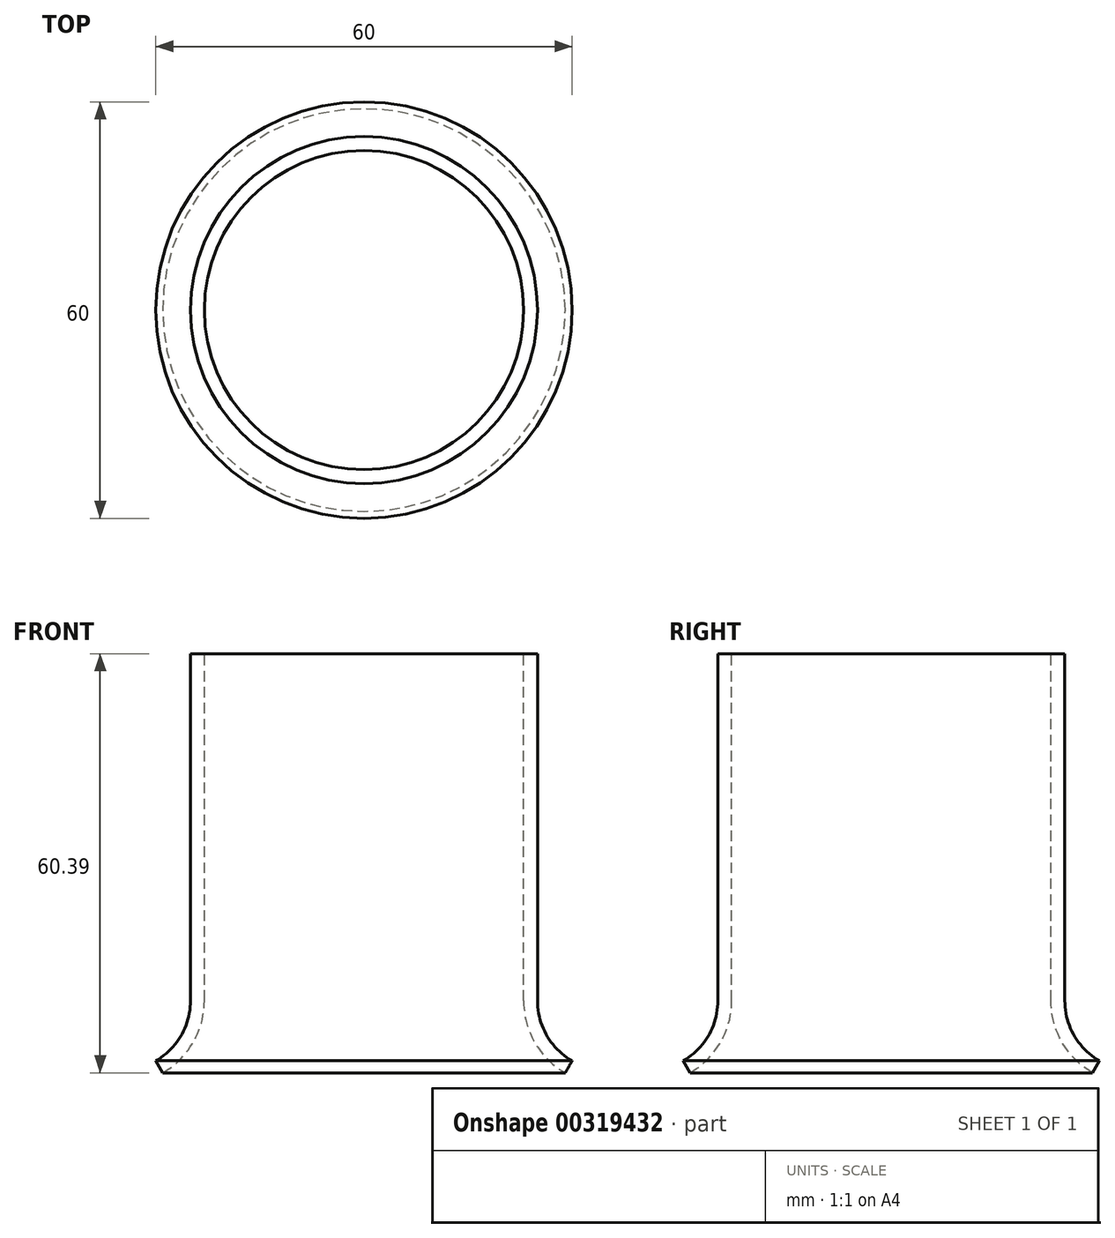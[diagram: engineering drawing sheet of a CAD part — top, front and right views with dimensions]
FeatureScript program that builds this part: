
annotation { "Feature Type Name" : "Feature", "Feature Type Description" : "" }
export const myFeature = defineFeature(function(context is Context, id is Id, definition is map)
    precondition{}
    {
        {
            var Q0;
            Q0=qCreatedBy(makeId("Front.planeOp"),FACE);
            var sketch = newSketch(context, id + "F0", { "sketchPlane" : qUnion([Q0])});
            skLineSegment(sketch, "E0", {"start": v(25, 0) * mm, "end": v(25, -50) * mm});
            skArc(sketch, "E1", {"start": v(25, -50) * mm, "mid": v(26.34, -55) * mm, "end": v(30, -58.66) * mm});
            skArc(sketch, "E2.0", {"start": v(23, -50) * mm, "mid": v(24.6, -56) * mm, "end": v(29, -60.4) * mm});
            skLineSegment(sketch, "E2.1", {"start": v(23, 0) * mm, "end": v(23, -50) * mm});
            skLineSegment(sketch, "E3", {"start": v(23, 0) * mm, "end": v(25, 0) * mm});
            skLineSegment(sketch, "E4", {"start": v(29, -60.4) * mm, "end": v(30, -58.66) * mm});
            skSolve(sketch);
        }
        {
            var Q0;
            Q0=qCreatedBy(makeId("Front.planeOp"),FACE);
            var sketch = newSketch(context, id + "F1", { "sketchPlane" : qUnion([Q0])});
            skLineSegment(sketch, "E5", {"start": v(0, 0) * mm, "end": v(0, -25.5) * mm});
            skSolve(sketch);
        }
        {
            var Q0;
            Q0 = qSketchRegion(id + "F0", true);
            var Q1;
            Q1 = qBodyType(qCreatedBy(id + "F1" ,EDGE), BodyType.WIRE);
            revolve(context, id + "F2", {"entities" : qUnion([Q0]), "axis" : qUnion([Q1]), "revolveType" : RevolveType.FULL});
        }
    });
